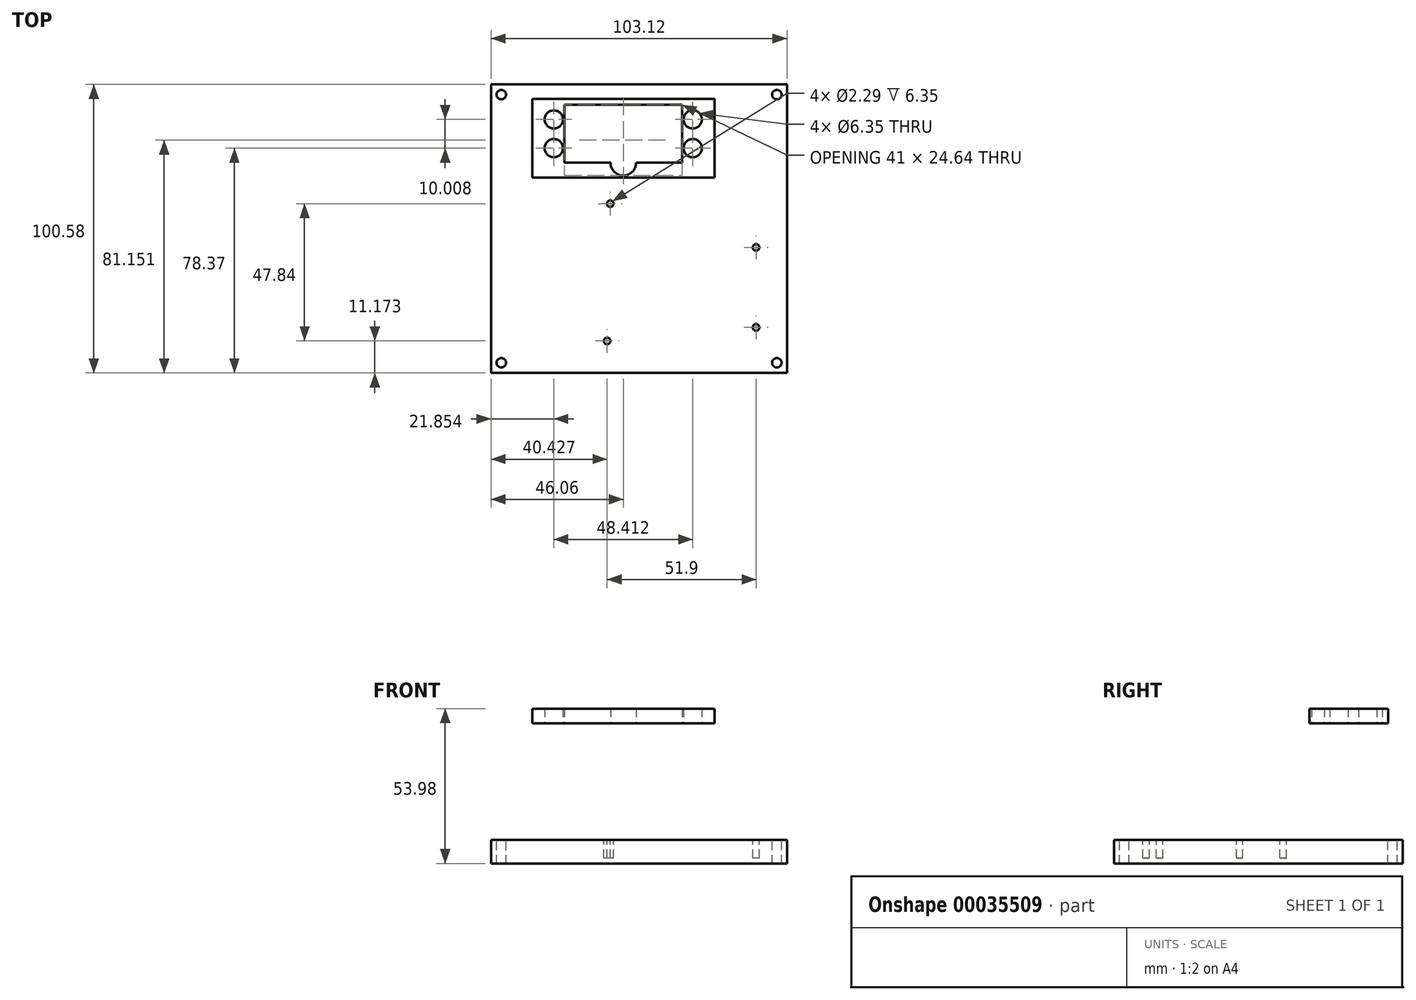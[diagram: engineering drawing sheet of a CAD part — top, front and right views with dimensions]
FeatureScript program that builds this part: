
annotation { "Feature Type Name" : "Feature", "Feature Type Description" : "" }
export const myFeature = defineFeature(function(context is Context, id is Id, definition is map)
    precondition{}
    {
        {
            var Q0;
            Q0=qCreatedBy(makeId("Top.planeOp"),FACE);
            var sketch = newSketch(context, id + "F0", { "sketchPlane" : qUnion([Q0])});
            skLineSegment(sketch, "E0.rect.bottom", {"start": v(57.15, 57.15) * mm, "end": v(-57.15, 57.15) * mm});
            skLineSegment(sketch, "E0.rect.top", {"start": v(57.15, -57.15) * mm, "end": v(-57.15, -57.15) * mm});
            skLineSegment(sketch, "E0.rect.left", {"start": v(57.15, 57.15) * mm, "end": v(57.15, -57.15) * mm});
            skLineSegment(sketch, "E0.rect.right", {"start": v(-57.15, 57.15) * mm, "end": v(-57.15, -57.15) * mm});
            skPoint(sketch, "E0.rect.middle", {"position": v(0, 0) * mm});
            skLineSegment(sketch, "E1.bottom", {"start": v(-26, 43.18) * mm, "end": v(15, 43.18) * mm});
            skLineSegment(sketch, "E1.top", {"start": v(-26, 22.99) * mm, "end": v(15, 22.99) * mm});
            skLineSegment(sketch, "E1.left", {"start": v(-26, 43.18) * mm, "end": v(-26, 22.99) * mm});
            skLineSegment(sketch, "E1.right", {"start": v(15, 43.18) * mm, "end": v(15, 22.99) * mm});
            skLineSegment(sketch, "E2", {"start": v(-5.5, 57.15) * mm, "end": v(-5.5, 43.18) * mm, "construction": true});
            skLineSegment(sketch, "E3.bottom", {"start": v(-29.7, 38.09) * mm, "end": v(18.7, 38.09) * mm, "construction": true});
            skLineSegment(sketch, "E3.top", {"start": v(-29.7, 28.08) * mm, "end": v(18.7, 28.08) * mm, "construction": true});
            skLineSegment(sketch, "E3.left", {"start": v(-29.7, 38.09) * mm, "end": v(-29.7, 28.08) * mm, "construction": true});
            skLineSegment(sketch, "E3.right", {"start": v(18.7, 38.09) * mm, "end": v(18.7, 28.08) * mm, "construction": true});
            skLineSegment(sketch, "E4", {"start": v(15, 33.08) * mm, "end": v(-26, 33.08) * mm, "construction": true});
            skCircle(sketch, "E5", {"center": v(18.7, 38.09) * mm, "radius": 3.18 * mm});
            skCircle(sketch, "E6", {"center": v(18.7, 28.08) * mm, "radius": 3.18 * mm});
            skCircle(sketch, "E7", {"center": v(-29.7, 28.08) * mm, "radius": 3.18 * mm});
            skCircle(sketch, "E8", {"center": v(-29.7, 38.09) * mm, "radius": 3.18 * mm});
            skCircle(sketch, "E9", {"center": v(-5.5, 22.99) * mm, "radius": 4.45 * mm});
            skLineSegment(sketch, "E10", {"start": v(-5.5, 57.15) * mm, "end": v(0, 57.15) * mm});
            skSolve(sketch);
        }
        {
            var Q0;
            Q0=qSketchRegion(id+"F0",true);
            extrude(context, id + "F1", {"entities" : qUnion([Q0]), "endBound" : BoundingType.SYMMETRIC, "depth" : 5.08 * mm});
        }
        {
            var Q0;
            Q0=makeQuery(id+"F1.opExtrude","CAP_FACE",FACE,{"disambiguationData":[OSD([sQuery(id+"F0.wireOp",EDGE,"E0.rect.bottom"),sQuery(id+"F0.wireOp",EDGE,"E0.rect.top"),sQuery(id+"F0.wireOp",EDGE,"E0.rect.left"),sQuery(id+"F0.wireOp",EDGE,"E0.rect.right"),sQuery(id+"F0.wireOp",EDGE,"E1.bottom"),sQuery(id+"F0.wireOp",EDGE,"E1.top"),sQuery(id+"F0.wireOp",EDGE,"E1.left"),sQuery(id+"F0.wireOp",EDGE,"E1.right"),sQuery(id+"F0.wireOp",EDGE,"E5"),sQuery(id+"F0.wireOp",EDGE,"E6"),sQuery(id+"F0.wireOp",EDGE,"E7"),sQuery(id+"F0.wireOp",EDGE,"E8")])],"isStart":true});
            var sketch = newSketch(context, id + "F2", { "sketchPlane" : qUnion([Q0])});
            skLineSegment(sketch, "E11.rect.bottom", {"start": v(57.15, 57.15) * mm, "end": v(-57.15, 57.15) * mm});
            skLineSegment(sketch, "E11.rect.top", {"start": v(57.15, -57.15) * mm, "end": v(-57.15, -57.15) * mm});
            skLineSegment(sketch, "E11.rect.left", {"start": v(57.15, 57.15) * mm, "end": v(57.15, -57.15) * mm});
            skLineSegment(sketch, "E11.rect.right", {"start": v(-57.15, 57.15) * mm, "end": v(-57.15, -57.15) * mm});
            skPoint(sketch, "E11.rect.middle", {"position": v(0, 0) * mm});
            skLineSegment(sketch, "E12.rect.bottom", {"start": v(52.07, 50.8) * mm, "end": v(-52.07, 50.8) * mm});
            skLineSegment(sketch, "E12.rect.top", {"start": v(52.07, -50.8) * mm, "end": v(-52.07, -50.8) * mm});
            skLineSegment(sketch, "E12.rect.left", {"start": v(52.07, 50.8) * mm, "end": v(52.07, -50.8) * mm});
            skLineSegment(sketch, "E12.rect.right", {"start": v(-52.07, 50.8) * mm, "end": v(-52.07, -50.8) * mm});
            skSolve(sketch);
        }
        {
            var Q0;
            Q0=qSketchRegion(id+"F2",true);
            extrude(context, id + "F3", {"entities" : qUnion([Q0]), "operationType" : NewBodyOperationType.ADD, "depth" : 3.17 * mm});
        }
        {
            var Q0;
            Q0=makeQuery(id+"F1.opExtrude","CAP_FACE",FACE,{"disambiguationData":[OSD([sQuery(id+"F0.wireOp",EDGE,"E0.rect.bottom"),sQuery(id+"F0.wireOp",EDGE,"E0.rect.top"),sQuery(id+"F0.wireOp",EDGE,"E0.rect.left"),sQuery(id+"F0.wireOp",EDGE,"E0.rect.right"),sQuery(id+"F0.wireOp",EDGE,"E1.bottom"),sQuery(id+"F0.wireOp",EDGE,"E1.top"),sQuery(id+"F0.wireOp",EDGE,"E1.left"),sQuery(id+"F0.wireOp",EDGE,"E1.right"),sQuery(id+"F0.wireOp",EDGE,"E5"),sQuery(id+"F0.wireOp",EDGE,"E6"),sQuery(id+"F0.wireOp",EDGE,"E7"),sQuery(id+"F0.wireOp",EDGE,"E8")])],"isStart":true});
            var sketch = newSketch(context, id + "F4", { "sketchPlane" : qUnion([Q0])});
            skLineSegment(sketch, "E13.rect.bottom", {"start": v(51.56, 50.3) * mm, "end": v(-51.56, 50.3) * mm});
            skLineSegment(sketch, "E13.rect.top", {"start": v(51.56, -50.3) * mm, "end": v(-51.56, -50.3) * mm});
            skLineSegment(sketch, "E13.rect.left", {"start": v(51.56, 50.3) * mm, "end": v(51.56, -50.3) * mm});
            skLineSegment(sketch, "E13.rect.right", {"start": v(-51.56, 50.3) * mm, "end": v(-51.56, -50.3) * mm});
            skPoint(sketch, "E13.rect.middle", {"position": v(0, 0) * mm});
            skLineSegment(sketch, "E14.rect.bottom", {"start": v(46.48, 45.21) * mm, "end": v(-46.48, 45.21) * mm});
            skLineSegment(sketch, "E14.rect.top", {"start": v(46.48, -45.21) * mm, "end": v(-46.48, -45.21) * mm});
            skLineSegment(sketch, "E14.rect.left", {"start": v(46.48, 45.21) * mm, "end": v(46.48, -45.21) * mm});
            skLineSegment(sketch, "E14.rect.right", {"start": v(-46.48, 45.21) * mm, "end": v(-46.48, -45.21) * mm});
            skSolve(sketch);
        }
        {
            var Q0;
            Q0=qSketchRegion(id+"F4",true);
            extrude(context, id + "F5", {"entities" : qUnion([Q0]), "depth" : 48.9 * mm});
        }
        {
            var Q0;
            Q0=makeQuery(id+"F5.opExtrude","CAP_FACE",FACE,{"disambiguationData":[OSD([sQuery(id+"F4.wireOp",EDGE,"E13.rect.bottom"),sQuery(id+"F4.wireOp",EDGE,"E13.rect.top"),sQuery(id+"F4.wireOp",EDGE,"E13.rect.left"),sQuery(id+"F4.wireOp",EDGE,"E13.rect.right"),sQuery(id+"F4.wireOp",EDGE,"E14.rect.bottom"),sQuery(id+"F4.wireOp",EDGE,"E14.rect.top"),sQuery(id+"F4.wireOp",EDGE,"E14.rect.left"),sQuery(id+"F4.wireOp",EDGE,"E14.rect.right")])],"isStart":false});
            var sketch = newSketch(context, id + "F6", { "sketchPlane" : qUnion([Q0])});
            skLineSegment(sketch, "E15.bottom", {"start": v(-51.56, 50.3) * mm, "end": v(51.56, 50.3) * mm});
            skLineSegment(sketch, "E15.top", {"start": v(-51.56, -50.3) * mm, "end": v(51.56, -50.3) * mm});
            skLineSegment(sketch, "E15.left", {"start": v(-51.56, 50.3) * mm, "end": v(-51.56, -50.3) * mm});
            skLineSegment(sketch, "E15.right", {"start": v(51.56, 50.3) * mm, "end": v(51.56, -50.3) * mm});
            skSolve(sketch);
        }
        {
            var Q0;
            Q0=qSketchRegion(id+"F6",true);
            extrude(context, id + "F7", {"entities" : qUnion([Q0]), "operationType" : NewBodyOperationType.ADD, "oppositeDirection" : true, "depth" : 8.25 * mm});
        }
        {
            var Q0;
            Q0=makeQuery(id+"F7.opExtrude","CAP_FACE",FACE,{"disambiguationData":[OSD([sQuery(id+"F6.wireOp",EDGE,"E15.bottom"),sQuery(id+"F6.wireOp",EDGE,"E15.top"),sQuery(id+"F6.wireOp",EDGE,"E15.left"),sQuery(id+"F6.wireOp",EDGE,"E15.right")])],"isStart":false});
            var sketch = newSketch(context, id + "F8", { "sketchPlane" : qUnion([Q0])});
            skPoint(sketch, "E16", {"position": v(-10.03, 8.72) * mm});
            skPoint(sketch, "E17", {"position": v(-11.13, -39.12) * mm});
            skPoint(sketch, "E18", {"position": v(40.77, -6.52) * mm});
            skPoint(sketch, "E19", {"position": v(40.77, -34.42) * mm});
            skLineSegment(sketch, "E20.bottom", {"start": v(-25.27, 11.3) * mm, "end": v(43.3, 11.3) * mm, "construction": true});
            skLineSegment(sketch, "E20.top", {"start": v(-25.27, -42.04) * mm, "end": v(43.3, -42.04) * mm, "construction": true});
            skLineSegment(sketch, "E20.left", {"start": v(-25.27, 11.3) * mm, "end": v(-25.27, -42.04) * mm, "construction": true});
            skLineSegment(sketch, "E20.right", {"start": v(43.3, 11.3) * mm, "end": v(43.3, -42.04) * mm, "construction": true});
            skCircle(sketch, "E21", {"center": v(-10.03, 8.72) * mm, "radius": 1.14 * mm});
            skCircle(sketch, "E22", {"center": v(40.77, -6.52) * mm, "radius": 1.14 * mm});
            skCircle(sketch, "E23", {"center": v(40.77, -34.42) * mm, "radius": 1.14 * mm});
            skCircle(sketch, "E24", {"center": v(-11.13, -39.12) * mm, "radius": 1.14 * mm});
            skSolve(sketch);
        }
        {
            var Q0;
            Q0=qSketchRegion(id+"F8",true);
            extrude(context, id + "F9", {"entities" : qUnion([Q0]), "operationType" : NewBodyOperationType.REMOVE, "oppositeDirection" : true, "depth" : 6.35 * mm});
        }
        {
            var Q0;
            Q0=makeQuery(id+"F5.opExtrude","SWEPT_EDGE",EDGE,{"disambiguationData":[OSD([sQuery(id+"F4.wireOp",EDGE,"E14.rect.top"),sQuery(id+"F4.wireOp",EDGE,"E14.rect.right")])]});
            var Q1;
            Q1=makeQuery(id+"F5.opExtrude","SWEPT_EDGE",EDGE,{"disambiguationData":[OSD([sQuery(id+"F4.wireOp",EDGE,"E14.rect.top"),sQuery(id+"F4.wireOp",EDGE,"E14.rect.left")])]});
            var Q2;
            Q2=makeQuery(id+"F5.opExtrude","SWEPT_EDGE",EDGE,{"disambiguationData":[OSD([sQuery(id+"F4.wireOp",EDGE,"E14.rect.bottom"),sQuery(id+"F4.wireOp",EDGE,"E14.rect.left")])]});
            var Q3;
            Q3=makeQuery(id+"F5.opExtrude","SWEPT_EDGE",EDGE,{"disambiguationData":[OSD([sQuery(id+"F4.wireOp",EDGE,"E14.rect.bottom"),sQuery(id+"F4.wireOp",EDGE,"E14.rect.right")])]});
            fillet(context, id + "F10", {"entities" : qUnion([Q0, Q1, Q2, Q3]), "radius" : 6.35 * mm, "tangentPropagation" : true, "allowEdgeOverflow" : false});
        }
        {
            var Q0;
            Q0=makeQuery(id+"F5.opExtrude","CAP_FACE",FACE,{"disambiguationData":[OSD([sQuery(id+"F4.wireOp",EDGE,"E13.rect.bottom"),sQuery(id+"F4.wireOp",EDGE,"E13.rect.top"),sQuery(id+"F4.wireOp",EDGE,"E13.rect.left"),sQuery(id+"F4.wireOp",EDGE,"E13.rect.right"),sQuery(id+"F4.wireOp",EDGE,"E14.rect.bottom"),sQuery(id+"F4.wireOp",EDGE,"E14.rect.top"),sQuery(id+"F4.wireOp",EDGE,"E14.rect.left"),sQuery(id+"F4.wireOp",EDGE,"E14.rect.right")])],"isStart":true});
            var sketch = newSketch(context, id + "F11", { "sketchPlane" : qUnion([Q0])});
            skLineSegment(sketch, "E25.rect.bottom", {"start": v(48, 46.74) * mm, "end": v(-48, 46.74) * mm, "construction": true});
            skLineSegment(sketch, "E25.rect.top", {"start": v(48, -46.74) * mm, "end": v(-48, -46.74) * mm, "construction": true});
            skLineSegment(sketch, "E25.rect.left", {"start": v(48, 46.74) * mm, "end": v(48, -46.74) * mm, "construction": true});
            skLineSegment(sketch, "E25.rect.right", {"start": v(-48, 46.74) * mm, "end": v(-48, -46.74) * mm, "construction": true});
            skPoint(sketch, "E25.rect.middle", {"position": v(0, 0) * mm});
            skCircle(sketch, "E26", {"center": v(-48, 46.74) * mm, "radius": 1.14 * mm});
            skCircle(sketch, "E27", {"center": v(48, 46.74) * mm, "radius": 1.14 * mm});
            skCircle(sketch, "E28", {"center": v(48, -46.74) * mm, "radius": 1.14 * mm});
            skCircle(sketch, "E29", {"center": v(-48, -46.74) * mm, "radius": 1.14 * mm});
            skSolve(sketch);
        }
        {
            var Q0;
            Q0=qSketchRegion(id+"F11",true);
            extrude(context, id + "F12", {"entities" : qUnion([Q0]), "operationType" : NewBodyOperationType.REMOVE, "oppositeDirection" : true, "depth" : 12.7 * mm});
        }
        {
            var Q0;
            Q0=makeQuery(id+"F1.opExtrude","CAP_FACE",FACE,{"disambiguationData":[OSD([sQuery(id+"F0.wireOp",EDGE,"E0.rect.bottom"),sQuery(id+"F0.wireOp",EDGE,"E0.rect.top"),sQuery(id+"F0.wireOp",EDGE,"E0.rect.left"),sQuery(id+"F0.wireOp",EDGE,"E0.rect.right"),sQuery(id+"F0.wireOp",EDGE,"E1.bottom"),sQuery(id+"F0.wireOp",EDGE,"E1.top"),sQuery(id+"F0.wireOp",EDGE,"E1.left"),sQuery(id+"F0.wireOp",EDGE,"E1.right"),sQuery(id+"F0.wireOp",EDGE,"E5"),sQuery(id+"F0.wireOp",EDGE,"E6"),sQuery(id+"F0.wireOp",EDGE,"E7"),sQuery(id+"F0.wireOp",EDGE,"E8"),sQuery(id+"F0.wireOp",EDGE,"E9")])],"isStart":false});
            var sketch = newSketch(context, id + "F13", { "sketchPlane" : qUnion([Q0])});
            skPoint(sketch, "E30.0", {"position": v(-48, -46.74) * mm});
            skPoint(sketch, "E30.1", {"position": v(48, -46.74) * mm});
            skPoint(sketch, "E30.2", {"position": v(48, 46.74) * mm});
            skPoint(sketch, "E30.3", {"position": v(-48, 46.74) * mm});
            skCircle(sketch, "E31", {"center": v(-48, -46.74) * mm, "radius": 1.65 * mm});
            skCircle(sketch, "E32", {"center": v(-48, 46.74) * mm, "radius": 1.65 * mm});
            skCircle(sketch, "E33", {"center": v(48, 46.74) * mm, "radius": 1.65 * mm});
            skCircle(sketch, "E34", {"center": v(48, -46.74) * mm, "radius": 1.65 * mm});
            skSolve(sketch);
        }
        {
            var Q0;
            Q0=qSketchRegion(id+"F13",true);
            extrude(context, id + "F14", {"entities" : qUnion([Q0]), "operationType" : NewBodyOperationType.REMOVE, "endBound" : BoundingType.THROUGH_ALL, "oppositeDirection" : true, "depth" : 25.4 * mm});
        }
        {
            var Q0;
            Q0=makeQuery(id+"F1.opExtrude","CAP_FACE",FACE,{"disambiguationData":[OSD([sQuery(id+"F0.wireOp",EDGE,"E0.rect.bottom"),sQuery(id+"F0.wireOp",EDGE,"E0.rect.top"),sQuery(id+"F0.wireOp",EDGE,"E0.rect.left"),sQuery(id+"F0.wireOp",EDGE,"E0.rect.right"),sQuery(id+"F0.wireOp",EDGE,"E1.bottom"),sQuery(id+"F0.wireOp",EDGE,"E1.top"),sQuery(id+"F0.wireOp",EDGE,"E1.left"),sQuery(id+"F0.wireOp",EDGE,"E1.right"),sQuery(id+"F0.wireOp",EDGE,"E5"),sQuery(id+"F0.wireOp",EDGE,"E6"),sQuery(id+"F0.wireOp",EDGE,"E7"),sQuery(id+"F0.wireOp",EDGE,"E8"),sQuery(id+"F0.wireOp",EDGE,"E9"),sQuery(id+"F0.wireOp",EDGE,"E10")])],"isStart":false});
            var sketch = newSketch(context, id + "F15", { "sketchPlane" : qUnion([Q0])});
            skLineSegment(sketch, "E35.rect.bottom", {"start": v(57.15, 57.15) * mm, "end": v(-57.15, 57.15) * mm});
            skLineSegment(sketch, "E35.rect.top", {"start": v(57.15, -57.15) * mm, "end": v(-57.15, -57.15) * mm});
            skLineSegment(sketch, "E35.rect.left", {"start": v(57.15, 57.15) * mm, "end": v(57.15, -57.15) * mm});
            skLineSegment(sketch, "E35.rect.right", {"start": v(-57.15, 57.15) * mm, "end": v(-57.15, -57.15) * mm});
            skPoint(sketch, "E35.rect.middle", {"position": v(0, 0) * mm});
            skLineSegment(sketch, "E36", {"start": v(-26, 22.99) * mm, "end": v(15, 43.18) * mm, "construction": true});
            skLineSegment(sketch, "E37.rect.bottom", {"start": v(26.25, 48.32) * mm, "end": v(-37.25, 48.32) * mm});
            skLineSegment(sketch, "E37.rect.top", {"start": v(26.25, 17.84) * mm, "end": v(-37.25, 17.84) * mm});
            skLineSegment(sketch, "E37.rect.left", {"start": v(26.25, 48.32) * mm, "end": v(26.25, 17.84) * mm});
            skLineSegment(sketch, "E37.rect.right", {"start": v(-37.25, 48.32) * mm, "end": v(-37.25, 17.84) * mm});
            skPoint(sketch, "E37.rect.middle", {"position": v(-5.5, 33.08) * mm});
            skSolve(sketch);
        }
        {
            var Q0;
            Q0 = qSketchRegion(id + "F15", true);
            var Q1;
            Q1=makeQuery(id+"F7.opExtrude","CAP_FACE",FACE,{"disambiguationData":[OSD([sQuery(id+"F6.wireOp",EDGE,"E15.bottom"),sQuery(id+"F6.wireOp",EDGE,"E15.top"),sQuery(id+"F6.wireOp",EDGE,"E15.left"),sQuery(id+"F6.wireOp",EDGE,"E15.right")])],"isStart":false});
            extrude(context, id + "F16", {"entities" : qUnion([Q0]), "operationType" : NewBodyOperationType.REMOVE, "endBound" : BoundingType.UP_TO_SURFACE, "oppositeDirection" : true, "endBoundEntityFace" : qUnion([Q1]), "depth" : 25.4 * mm});
        }
        {
            var Q0;
            Q0=makeQuery(id+"F16.boolean.opBoolean","MERGE",FACE,{"derivedFrom":[makeQuery(id+"F7.opExtrude","CAP_FACE",FACE,{"disambiguationData":[OSD([sQuery(id+"F6.wireOp",EDGE,"E15.bottom"),sQuery(id+"F6.wireOp",EDGE,"E15.top"),sQuery(id+"F6.wireOp",EDGE,"E15.left"),sQuery(id+"F6.wireOp",EDGE,"E15.right")])],"isStart":false}),makeQuery(id+"F16.opExtrude","CAP_FACE",FACE,{"disambiguationData":[OSD([sQuery(id+"F15.wireOp",EDGE,"E35.rect.bottom"),sQuery(id+"F15.wireOp",EDGE,"E35.rect.top"),sQuery(id+"F15.wireOp",EDGE,"E35.rect.left"),sQuery(id+"F15.wireOp",EDGE,"E35.rect.right"),sQuery(id+"F15.wireOp",EDGE,"E37.rect.bottom"),sQuery(id+"F15.wireOp",EDGE,"E37.rect.top"),sQuery(id+"F15.wireOp",EDGE,"E37.rect.left"),sQuery(id+"F15.wireOp",EDGE,"E37.rect.right")])],"isStart":false})]});
            var sketch = newSketch(context, id + "F17", { "sketchPlane" : qUnion([Q0])});
            skLineSegment(sketch, "E38.0.0", {"start": v(-37.25, 45.21) * mm, "end": v(26.25, 45.21) * mm});
            skLineSegment(sketch, "E38.0.1", {"start": v(26.25, 45.21) * mm, "end": v(26.25, 48.32) * mm});
            skLineSegment(sketch, "E38.0.2", {"start": v(26.25, 48.32) * mm, "end": v(-37.25, 48.32) * mm});
            skLineSegment(sketch, "E38.0.3", {"start": v(-37.25, 48.32) * mm, "end": v(-37.25, 45.21) * mm});
            skSolve(sketch);
        }
        {
            var Q0;
            Q0 = qSketchRegion(id + "F17", true);
            extrude(context, id + "F18", {"entities" : qUnion([Q0]), "operationType" : NewBodyOperationType.REMOVE, "endBound" : BoundingType.THROUGH_ALL, "depth" : 25.4 * mm});
        }
    });
